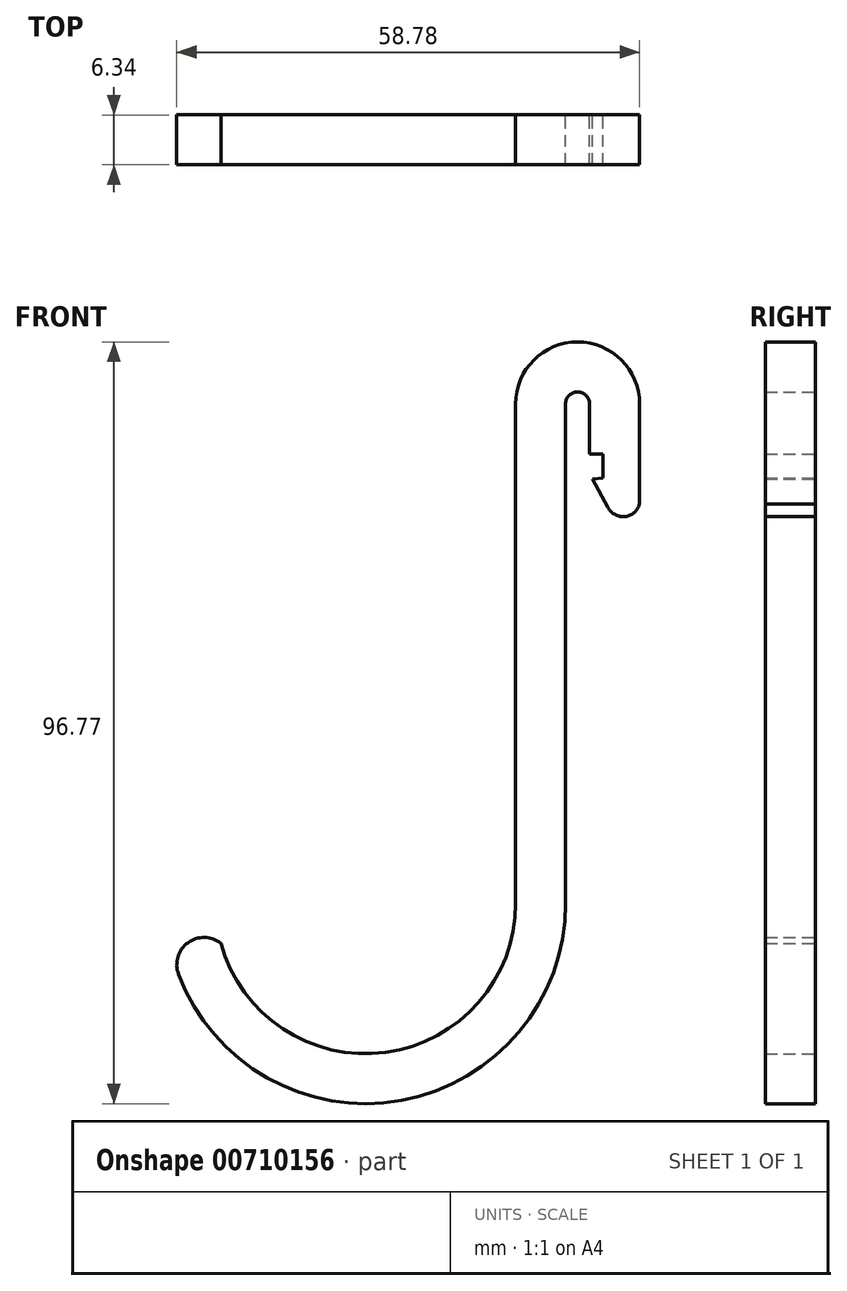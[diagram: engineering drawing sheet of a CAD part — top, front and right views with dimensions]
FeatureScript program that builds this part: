
annotation { "Feature Type Name" : "Feature", "Feature Type Description" : "" }
export const myFeature = defineFeature(function(context is Context, id is Id, definition is map)
    precondition{}
    {
        {
            var Q0;
            Q0=qCreatedBy(makeId("Front.planeOp"),FACE);
            var sketch = newSketch(context, id + "F0", { "sketchPlane" : qUnion([Q0])});
            skLineSegment(sketch, "E0", {"start": v(-2.34, 12.7) * mm, "end": v(-2.34, -50.8) * mm});
            skArc(sketch, "E1", {"start": v(-2.34, -50.8) * mm, "mid": v(-23.19, -75.79) * mm, "end": v(-51.5, -59.77) * mm});
            skArc(sketch, "E2", {"start": v(-2.34, 12.7) * mm, "mid": v(-0.82, 14.22) * mm, "end": v(0.7, 12.7) * mm});
            skArc(sketch, "E3.0", {"start": v(-8.7, -50.8) * mm, "mid": v(-25.2, -69.68) * mm, "end": v(-46.12, -55.83) * mm});
            skLineSegment(sketch, "E3.1", {"start": v(-8.7, 12.7) * mm, "end": v(-8.7, -50.8) * mm});
            skArc(sketch, "E3.2", {"start": v(-8.7, 12.7) * mm, "mid": v(-0.82, 20.57) * mm, "end": v(7.05, 12.7) * mm});
            skLineSegment(sketch, "E3.3", {"start": v(7.05, 0) * mm, "end": v(7.05, 12.7) * mm});
            skArc(sketch, "E4", {"start": v(-51.5, -59.77) * mm, "mid": v(-50.31, -55.75) * mm, "end": v(-46.12, -55.83) * mm});
            skLineSegment(sketch, "E5", {"start": v(0.7, 12.7) * mm, "end": v(0.7, 6.35) * mm});
            skLineSegment(sketch, "E6", {"start": v(0.7, 6.35) * mm, "end": v(2.43, 6.35) * mm});
            skLineSegment(sketch, "E7", {"start": v(2.43, 6.35) * mm, "end": v(2.43, 3.3) * mm});
            skLineSegment(sketch, "E8", {"start": v(2.43, 3.3) * mm, "end": v(1.07, 3.18) * mm});
            skLineSegment(sketch, "E9", {"start": v(1.07, 3.18) * mm, "end": v(3.07, -0.5) * mm});
            skArc(sketch, "E10", {"start": v(3.07, -0.5) * mm, "mid": v(5.23, -1.61) * mm, "end": v(7.05, 0) * mm});
            skSolve(sketch);
        }
        {
            var Q0;
            Q0=makeQuery(id+"F0.imprint","IMPRINT",FACE,{"disambiguationData":[TD([[makeQuery(id+"F0.imprint","IMPRINT",EDGE,{"derivedFrom":sQuery(id+"F0.wireOp",EDGE,"E0")}),-1.0]])]});
            extrude(context, id + "F1", {"entities" : qUnion([Q0]), "endBound" : BoundingType.SYMMETRIC, "depth" : 6.35 * mm, "offsetDistance" : 25.4 * mm});
        }
    });
